# Revit family: ERA_Вентилятор_MARS
name_source: partatom
category: Оборудование
units: mm (PartAtom-declared; Revit-internal decimal feet)

## family parameters
Всегда вертикально = Да
Классификация = Нет
На основе рабочей плоскости = Нет
Общий = Нет
При загрузке вырезать с полостями = Нет
Размер круглого соединителя = Использовать диаметр
Тип детали = Вставляется
Точка расчета площади = Нет

## types (7) — shared parameters
ADSK_URL документации изделия = https://era.trade
ADSK_URL страницы изделия = https://era.trade
ADSK_Версия Revit = 2019
ADSK_Версия семейства = Ver.1 2025-02
ADSK_Единица измерения = шт.
ADSK_Завод-изготовитель = ООО «ЭРА»
ADSK_Классификация нагрузок = Электродвигатель вентилятора
ADSK_Количество = 1
ADSK_Количество фаз = 1
ADSK_Количество фаз числовое = 1
ADSK_Коэффициент мощности = 0.8
ADSK_Материал = ERA_Пластик_Серебристый
ADSK_Напряжение = 230 В
ERA_IP вентилятора = X4
ERA_IP двигателя = 44
ERA_Гарантия = 2 года
ERA_Количество в транспортной упаковке = 1
ERA_Контакты = 8 (4912) 70-16-76, 8 (4912) 24-16-00
ERA_Материал корпуса = Оцинкованная сталь
ERA_Материал лопастей = Композитный пластик
ERA_Принцип вентиляции = Приточно-вытяжной
ERA_Рабочий механизм = Центробежный
ERA_Размещение = Канальное
ERA_Страна производитель = Россия
ERA_Температурный диапазон работы = от минус 25°С до плюс 70 °С
ERA_Торговая марка = ERA PRO
ERA_Управление = Механическое
ERA_Цвет = Серебристый
LT = ERA_Вентилятор_MARS
URL = https://era.trade
Изготовитель = ООО «ЭРА»
Производитель_Контакты_Телефон = 8 (4912) 70-16-76, 8 (4912) 24-16-00

## per-type parameters (varying)
| type | A | ADSK_Масса | ADSK_Масса_Текст | ADSK_Наименование | ADSK_Номинальная мощность | ADSK_Полная мощность | ADSK_Размер_Высота | ADSK_Размер_Диаметр | ADSK_Размер_Длина | ADSK_Размер_Ширина | ADSK_Ток | B | B1 | Code1 | D | D1 | ERA_Уровень шума | ERA_Частота вращения |
| MARS GDF 100 | 200 мм | 2.94 | 2.94 | Вентилятор канальный MARS GDF 100 | 62 Вт | 62 В·А | 243 мм | 100 мм | 200 мм | 243 мм | 0 А | 23 мм | 44 мм | 1 | 100 мм | 243 мм | 55 | 2587 |
| MARS GDF 125 | 202 мм | 2.93 | 2.93 | Вентилятор канальный MARS GDF 125 | 64 Вт | 64 В·А | 243 мм | 125 мм | 202 мм | 243 мм | 0 А | 27 мм | 44 мм | 2 | 125 мм | 243 мм | 54 | 2505 |
| MARS GDF 150 | 230 мм | 4.06 | 4.06 | Вентилятор канальный MARS GDF 150 | 101 Вт | 101 В·А | 333 мм | 150 мм | 230 мм | 333 мм | 0 А | 23 мм | 52 мм | 3 | 150 мм | 333 мм | 60 | 2605 |
| MARS GDF 160 | 235 мм | 4.1 | 4.1 | Вентилятор канальный MARS GDF 160 | 102 Вт | 102 В·А | 333 мм | 160 мм | 235 мм | 333 мм | 0 А | 25 мм | 53 мм | 4 | 160 мм | 333 мм | 60 | 2578 |
| MARS GDF 200 | 223 мм | 5 | 5 | Вентилятор канальный MARS GDF 200 | 144 Вт | 144 В·А | 333 мм | 200 мм | 223 мм | 333 мм | 1 А | 24 мм | 50 мм | 5 | 200 мм | 333 мм | 70 | 2654 |
| MARS GDF 250 | 205 мм | 5.43 | 5.43 | Вентилятор канальный MARS GDF 250 | 177 Вт | 177 В·А | 333 мм | 250 мм | 205 мм | 333 мм | 1 А | 27 мм | 45 мм | 6 | 250 мм | 333 мм | 60 | 2544 |
| MARS GDF 315 | 238 мм | 6.58 | 6.58 | Вентилятор канальный MARS GDF 315 | 278 Вт | 278 В·А | 402 мм | 315 мм | 238 мм | 402 мм | 1 А | 25 мм | 53 мм | 7 | 315 мм | 402 мм | 61 | 2502 |

note: column(s) folded — value = type name in every type: ADSK_Код изделия, ADSK_Марка, ADSK_Обозначение
